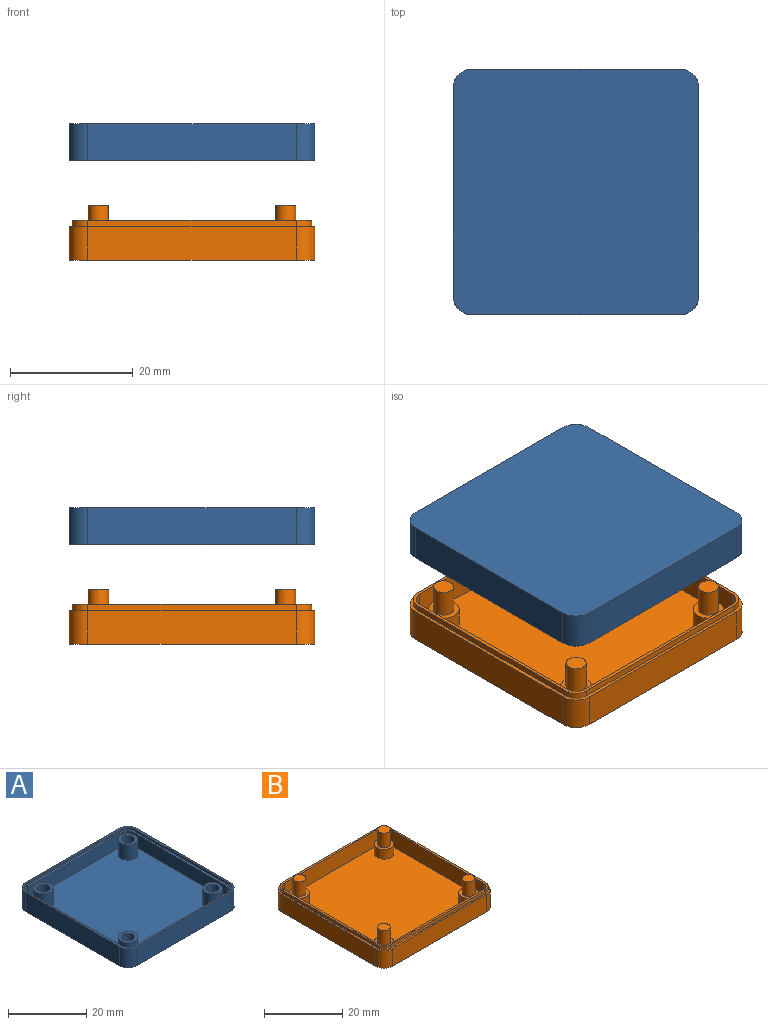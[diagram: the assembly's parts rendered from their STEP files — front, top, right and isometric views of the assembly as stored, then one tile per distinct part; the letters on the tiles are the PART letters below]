
ASSEMBLY  parts=2 mates=1
PART A: 44 faces, bbox 40x40x6 mm
  f0: cylinder r=1.75mm len=4.5mm, axis (0,0,-1), area 49.5mm2, adj f33,f43
  f1: cylinder r=1.75mm len=4.5mm, axis (0,0,-1), area 49.5mm2, adj f39,f42
  f2: cylinder r=1.75mm len=4.5mm, axis (0,0,-1), area 49.5mm2, adj f37,f41
  f3: cylinder r=1.75mm len=4.5mm, axis (0,0,-1), area 49.5mm2, adj f35,f40
  f4: plane 38.02x38mm, normal (0,0,1), area 1362.6mm2, adj f23,f24,f25,f26,f27,f28,f29,f30
  f5: plane 34.02x6mm, normal (1,0,0), area 204.1mm2, adj f6,f12,f13,f22
  f6: cylinder r=3mm len=6mm, axis (0,0,-1), area 28.3mm2, adj f5,f7,f13,f22
  f7: plane 34x6mm, normal (0,-1,0), area 204mm2, adj f6,f8,f13,f22
  f8: cylinder r=3mm len=6mm, axis (0,0,-1), area 28.3mm2, adj f7,f9,f13,f22
  f9: plane 34.02x6mm, normal (-1,0,0), area 204.1mm2, adj f8,f10,f13,f22
  f10: cylinder r=3mm len=6mm, axis (0,0,-1), area 28.3mm2, adj f9,f11,f13,f22
  f11: plane 34x6mm, normal (0,1,0), area 204mm2, adj f10,f12,f13,f22
  f12: cylinder r=3mm len=6mm, axis (0,0,-1), area 28.3mm2, adj f5,f11,f13,f22
  f13: plane 40.02x40mm, normal (0,0,-1), area 1592.9mm2, adj f5,f6,f7,f8,f9,f10,f11,f12
  f14: cylinder r=2.5mm len=2.5mm, axis (0,0,-1), area 2.9mm2, adj f15,f21,f22,f31
  f15: plane 34.02x0.75mm, normal (-1,0,0), area 25.5mm2, adj f14,f16,f22,f31
  f16: cylinder r=2.5mm len=2.5mm, axis (0,0,-1), area 2.9mm2, adj f15,f17,f22,f31
  f17: plane 34x0.75mm, normal (0,-1,0), area 25.5mm2, adj f16,f18,f22,f31
  f18: cylinder r=2.5mm len=2.5mm, axis (0,0,-1), area 2.9mm2, adj f17,f19,f22,f31
  f19: plane 34.02x0.75mm, normal (1,0,0), area 25.5mm2, adj f18,f20,f22,f31
  f20: cylinder r=2.5mm len=2.5mm, axis (0,0,-1), area 2.9mm2, adj f19,f21,f22,f31
  f21: plane 34x0.75mm, normal (0,1,0), area 25.5mm2, adj f14,f20,f22,f31
  f22: plane 40.02x40mm, normal (0,0,1), area 76.7mm2, adj f5,f6,f7,f8,f9,f10,f11,f12
  f23: cylinder r=2mm len=4.25mm, axis (0,0,-1), area 13.4mm2, adj f4,f24,f30,f31
  f24: plane 34.02x4.25mm, normal (-1,0,0), area 144.6mm2, adj f4,f23,f25,f31
  f25: cylinder r=2mm len=4.25mm, axis (0,0,-1), area 13.4mm2, adj f4,f24,f26,f31
  f26: plane 34x4.25mm, normal (0,-1,0), area 144.5mm2, adj f4,f25,f27,f31
  f27: cylinder r=2mm len=4.25mm, axis (0,0,-1), area 13.4mm2, adj f4,f26,f28,f31
  f28: plane 34.02x4.25mm, normal (1,0,0), area 144.6mm2, adj f4,f27,f29,f31
  f29: cylinder r=2mm len=4.25mm, axis (0,0,-1), area 13.4mm2, adj f4,f28,f30,f31
  f30: plane 34x4.25mm, normal (0,1,0), area 144.5mm2, adj f4,f23,f29,f31
  f31: plane 39.02x39mm, normal (0,0,1), area 75.1mm2, adj f14,f15,f16,f17,f18,f19,f20,f21
  f32: cylinder r=2.5mm len=5mm, axis (0,0,-1), area 74.6mm2, adj f4,f33
  f33: plane 5x5mm, normal (0,0,1), area 10mm2, adj f0,f32
  f34: cylinder r=2.5mm len=5mm, axis (0,0,-1), area 74.6mm2, adj f4,f35
  f35: plane 5x5mm, normal (0,0,1), area 10mm2, adj f3,f34
  f36: cylinder r=2.5mm len=5mm, axis (0,0,-1), area 74.6mm2, adj f4,f37
  f37: plane 5x5mm, normal (0,0,1), area 10mm2, adj f2,f36
  f38: cylinder r=2.5mm len=5mm, axis (0,0,-1), area 74.6mm2, adj f4,f39
  f39: plane 5x5mm, normal (0,0,1), area 10mm2, adj f1,f38
  f40: plane 3.5x3.5mm, normal (0,0,1), area 9.6mm2, adj f3
  f41: plane 3.5x3.5mm, normal (0,0,1), area 9.6mm2, adj f2
  f42: plane 3.5x3.5mm, normal (0,0,1), area 9.6mm2, adj f1
  f43: plane 3.5x3.5mm, normal (0,0,1), area 9.6mm2, adj f0
PART B: 44 faces, bbox 40x40x9 mm
  f0: cylinder r=2mm len=5mm, axis (0,0,-1), area 15.7mm2, adj f1,f7,f16,f27
  f1: plane 34x5mm, normal (0,1,0), area 170mm2, adj f0,f2,f16,f27
  f2: cylinder r=2mm len=5mm, axis (0,0,-1), area 15.7mm2, adj f1,f3,f16,f27
  f3: plane 34x5mm, normal (-1,0,0), area 170mm2, adj f2,f4,f16,f27
  f4: cylinder r=2mm len=5mm, axis (0,0,-1), area 15.7mm2, adj f3,f5,f16,f27
  f5: plane 34x5mm, normal (0,-1,0), area 170mm2, adj f4,f6,f16,f27
  f6: cylinder r=2mm len=5mm, axis (0,0,-1), area 15.7mm2, adj f5,f7,f16,f27
  f7: plane 34x5mm, normal (1,0,0), area 170mm2, adj f0,f6,f16,f27
  f8: plane 34x1mm, normal (0,-1,0), area 34mm2, adj f9,f15,f16,f26
  f9: cylinder r=2.5mm len=2.5mm, axis (0,0,-1), area 3.9mm2, adj f8,f10,f16,f26
  f10: plane 34x1mm, normal (-1,0,0), area 34mm2, adj f9,f11,f16,f26
  f11: cylinder r=2.5mm len=2.5mm, axis (0,0,-1), area 3.9mm2, adj f10,f12,f16,f26
  f12: plane 34x1mm, normal (0,1,0), area 34mm2, adj f11,f13,f16,f26
  f13: cylinder r=2.5mm len=2.5mm, axis (0,0,-1), area 3.9mm2, adj f12,f14,f16,f26
  f14: plane 34x1mm, normal (1,0,0), area 34mm2, adj f13,f15,f16,f26
  f15: cylinder r=2.5mm len=2.5mm, axis (0,0,-1), area 3.9mm2, adj f8,f14,f16,f26
  f16: plane 39x39mm, normal (0,0,1), area 75.1mm2, adj f0,f1,f2,f3,f4,f5,f6,f7
  f17: plane 40x40mm, normal (0,0,-1), area 1592.3mm2, adj f18,f19,f20,f21,f22,f23,f24,f25
  f18: plane 34x5.5mm, normal (1,0,0), area 187mm2, adj f17,f19,f25,f26
  f19: cylinder r=3mm len=5.5mm, axis (0,0,-1), area 25.9mm2, adj f17,f18,f20,f26
  f20: plane 34x5.5mm, normal (0,-1,0), area 187mm2, adj f17,f19,f21,f26
  f21: cylinder r=3mm len=5.5mm, axis (0,0,-1), area 25.9mm2, adj f17,f20,f22,f26
  f22: plane 34x5.5mm, normal (-1,0,0), area 187mm2, adj f17,f21,f23,f26
  f23: cylinder r=3mm len=5.5mm, axis (0,0,-1), area 25.9mm2, adj f17,f22,f24,f26
  f24: plane 34x5.5mm, normal (0,1,0), area 187mm2, adj f17,f23,f25,f26
  f25: cylinder r=3mm len=5.5mm, axis (0,0,-1), area 25.9mm2, adj f17,f18,f24,f26
  f26: plane 40x40mm, normal (0,0,1), area 76.6mm2, adj f8,f9,f10,f11,f12,f13,f14,f15
  f27: plane 38x38mm, normal (0,0,1), area 1362mm2, adj f0,f1,f2,f3,f4,f5,f6,f7
  f28: cylinder r=1.65mm len=4.5mm, axis (0,0,-1), area 46.7mm2, adj f29,f31
  f29: plane 3.3x3.3mm, normal (0,0,1), area 8.6mm2, adj f28
  f30: cylinder r=2.5mm len=5mm, axis (0,0,-1), area 47.1mm2, adj f27,f31
  f31: plane 5x5mm, normal (0,0,1), area 11.1mm2, adj f28,f30
  f32: cylinder r=1.65mm len=4.5mm, axis (0,0,-1), area 46.7mm2, adj f33,f35
  f33: plane 3.3x3.3mm, normal (0,0,1), area 8.6mm2, adj f32
  f34: cylinder r=2.5mm len=5mm, axis (0,0,-1), area 47.1mm2, adj f27,f35
  f35: plane 5x5mm, normal (0,0,1), area 11.1mm2, adj f32,f34
  f36: cylinder r=1.65mm len=4.5mm, axis (0,0,-1), area 46.7mm2, adj f37,f39
  f37: plane 3.3x3.3mm, normal (0,0,1), area 8.6mm2, adj f36
  f38: cylinder r=2.5mm len=5mm, axis (0,0,-1), area 47.1mm2, adj f27,f39
  f39: plane 5x5mm, normal (0,0,1), area 11.1mm2, adj f36,f38
  f40: cylinder r=1.65mm len=4.5mm, axis (0,0,-1), area 46.7mm2, adj f41,f43
  f41: plane 3.3x3.3mm, normal (0,0,1), area 8.6mm2, adj f40
  f42: cylinder r=2.5mm len=5mm, axis (0,0,-1), area 47.1mm2, adj f27,f43
  f43: plane 5x5mm, normal (0,0,1), area 11.1mm2, adj f40,f42
PLACE A rot(axis=(1,0,0),180deg) t=(0,44,22.5)mm
PLACE B at identity fixed
MATE slider A.f0 <-> B.f36  axis (0,0,1) through (-15.25,15.25,19)mm
